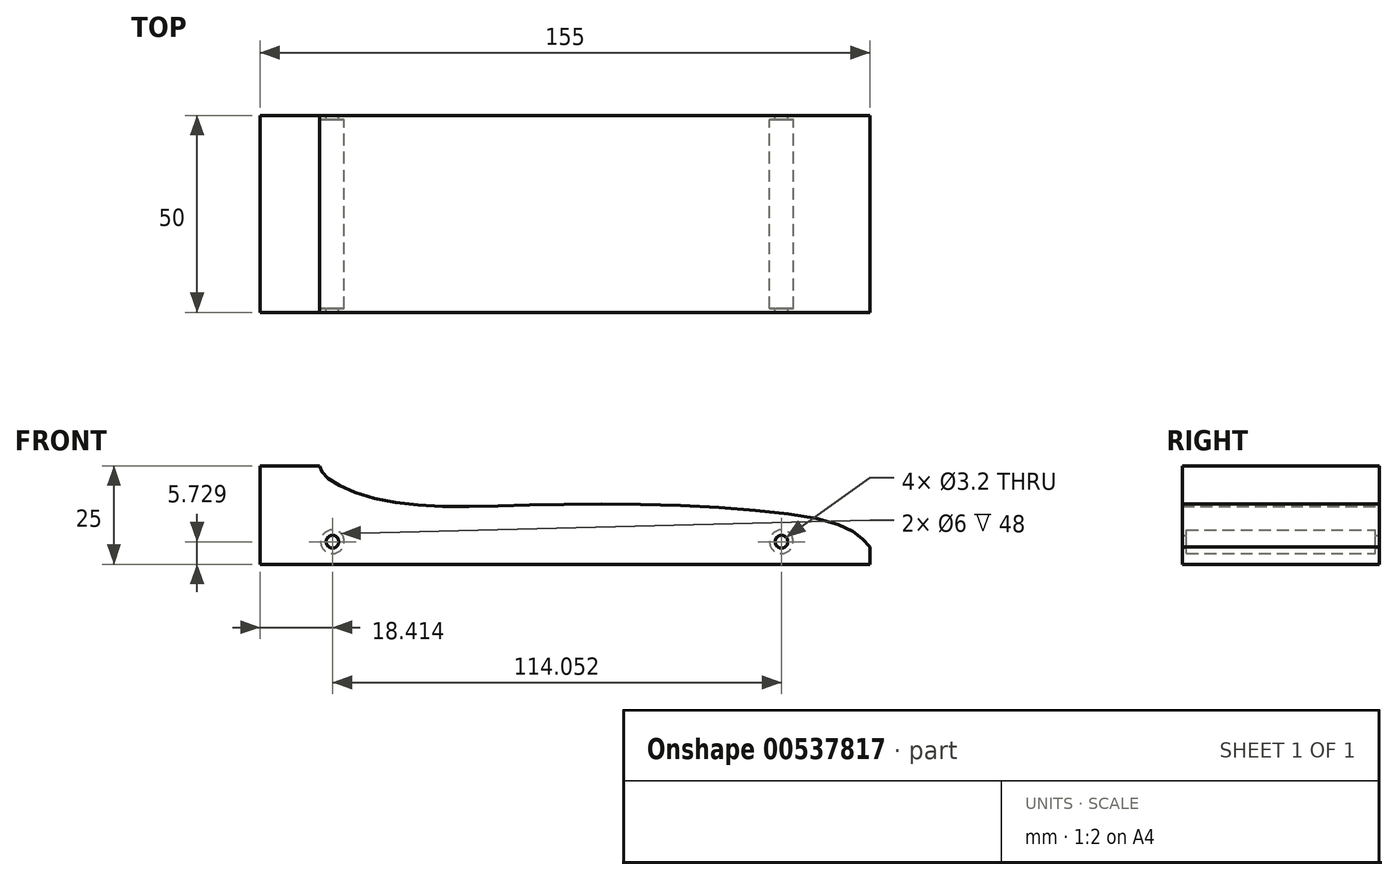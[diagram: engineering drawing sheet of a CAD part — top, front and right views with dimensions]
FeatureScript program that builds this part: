
annotation { "Feature Type Name" : "Feature", "Feature Type Description" : "" }
export const myFeature = defineFeature(function(context is Context, id is Id, definition is map)
    precondition{}
    {
        {
            var Q0;
            Q0=qCreatedBy(makeId("Front.planeOp"),FACE);
            var sketch = newSketch(context, id + "F0", { "sketchPlane" : qUnion([Q0])});
            skLineSegment(sketch, "E0.bottom", {"start": v(-76.83, 2.64) * mm, "end": v(78.17, 2.64) * mm});
            skLineSegment(sketch, "E0.top", {"start": v(-76.83, -22.36) * mm, "end": v(78.17, -22.36) * mm});
            skLineSegment(sketch, "E0.left", {"start": v(-76.83, 2.64) * mm, "end": v(-76.83, -22.36) * mm});
            skLineSegment(sketch, "E0.right", {"start": v(78.17, 2.64) * mm, "end": v(78.17, -22.36) * mm});
            skFitSpline(sketch, "E1", {"points": [v(78.17, -17.98) * mm, v(69.7, -12.15) * mm, v(0, -7.11) * mm, v(-44.83, -6.29) * mm, v(-60.23, 0) * mm, v(-61.7, 2.64) * mm], "startDerivative": vector(-41.18, 47.25) * mm, "endDerivative": vector(-10.6, 35.36) * mm});
            skPoint(sketch, "E2", {"position": v(-58.42, -16.63) * mm});
            skPoint(sketch, "E3", {"position": v(55.64, -16.63) * mm});
            skCircle(sketch, "E4", {"center": v(-58.42, -16.63) * mm, "radius": 3 * mm});
            skCircle(sketch, "E5", {"center": v(55.64, -16.63) * mm, "radius": 3 * mm});
            skCircle(sketch, "E6", {"center": v(-58.42, -16.63) * mm, "radius": 1.6 * mm});
            skCircle(sketch, "E7", {"center": v(55.64, -16.63) * mm, "radius": 1.6 * mm});
            skSolve(sketch);
        }
        {
            var Q0;
            {var subQ1=sQuery(id+"F0.wireOp",EDGE,"E0.top");Q0=makeQuery(id+"F0.imprint","IMPRINT",FACE,{"disambiguationData":[TD([[makeQuery(id+"F0.imprint","IMPRINT",EDGE,{"derivedFrom":subQ1}),1.0]])]});}
            var Q1;
            Q1=makeQuery(id+"F0.imprint","IMPRINT",FACE,{"disambiguationData":[TD([[makeQuery(id+"F0.imprint","IMPRINT",EDGE,{"derivedFrom":sQuery(id+"F0.wireOp",EDGE,"E4")}),1.0]])]});
            var Q2;
            Q2=makeQuery(id+"F0.imprint","IMPRINT",FACE,{"disambiguationData":[TD([[makeQuery(id+"F0.imprint","IMPRINT",EDGE,{"derivedFrom":sQuery(id+"F0.wireOp",EDGE,"E5")}),1.0]])]});
            extrude(context, id + "F1", {"entities" : qUnion([Q0, Q1, Q2]), "endBound" : BoundingType.SYMMETRIC, "depth" : 50 * mm, "offsetDistance" : 25 * mm});
        }
        {
            var Q0;
            Q0=makeQuery(id+"F0.imprint","IMPRINT",FACE,{"disambiguationData":[TD([[makeQuery(id+"F0.imprint","IMPRINT",EDGE,{"derivedFrom":sQuery(id+"F0.wireOp",EDGE,"E4")}),1.0]])]});
            extrude(context, id + "F2", {"entities" : qUnion([Q0]), "operationType" : NewBodyOperationType.REMOVE, "endBound" : BoundingType.SYMMETRIC, "depth" : 48 * mm, "offsetDistance" : 25 * mm});
        }
        {
            var Q0;
            Q0=makeQuery(id+"F0.imprint","IMPRINT",FACE,{"disambiguationData":[TD([[makeQuery(id+"F0.imprint","IMPRINT",EDGE,{"derivedFrom":sQuery(id+"F0.wireOp",EDGE,"E5")}),1.0]])]});
            extrude(context, id + "F3", {"entities" : qUnion([Q0]), "operationType" : NewBodyOperationType.REMOVE, "endBound" : BoundingType.SYMMETRIC, "depth" : 48 * mm, "offsetDistance" : 25 * mm});
        }
    });
